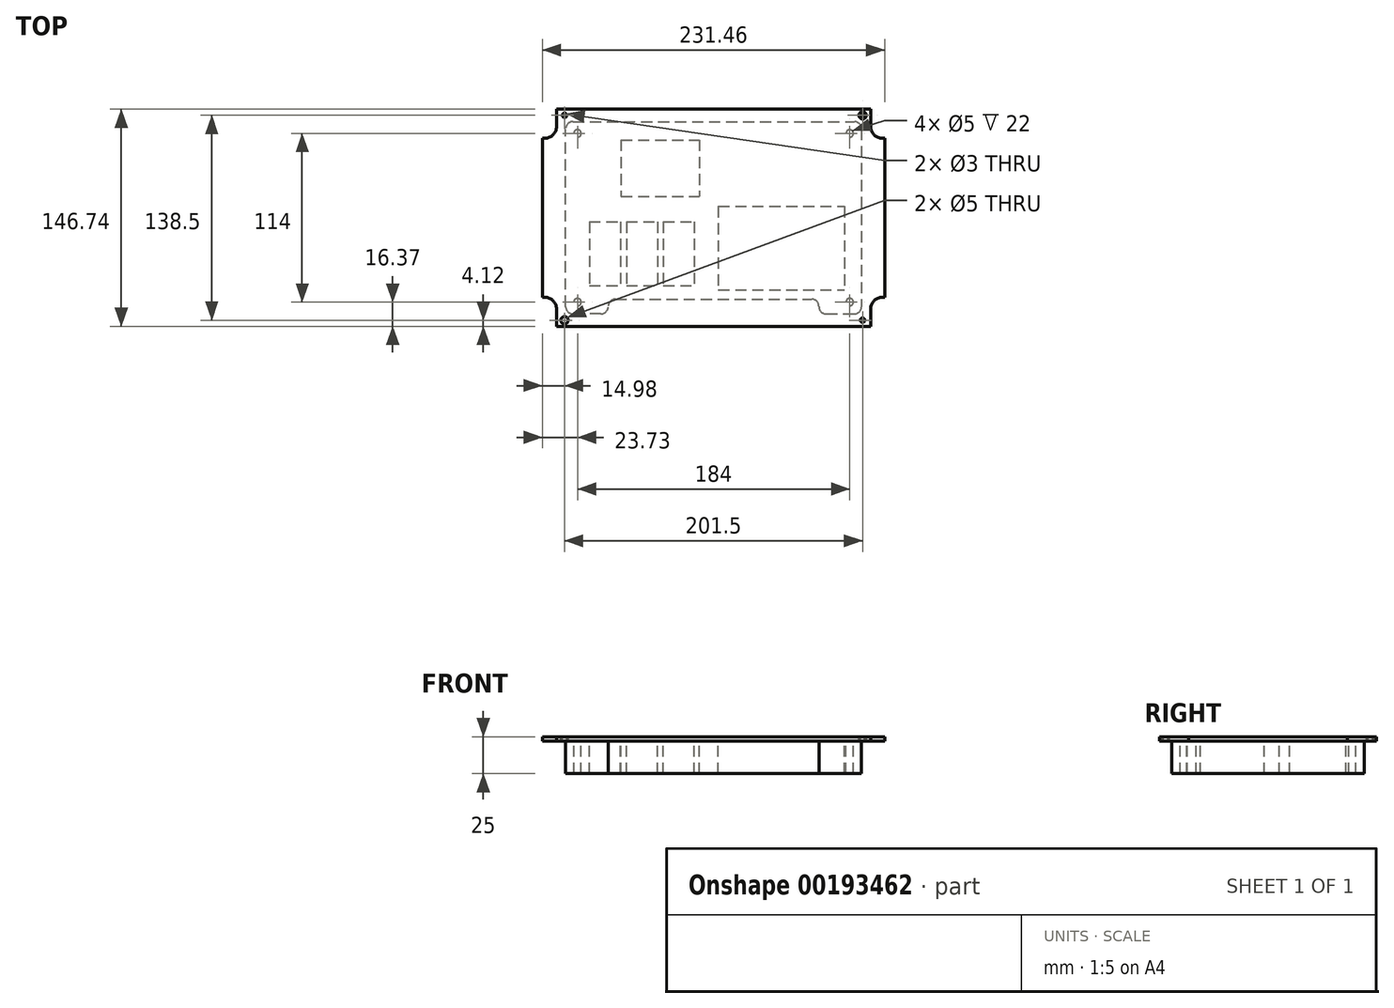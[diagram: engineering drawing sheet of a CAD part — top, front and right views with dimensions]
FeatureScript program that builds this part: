
annotation { "Feature Type Name" : "Feature", "Feature Type Description" : "" }
export const myFeature = defineFeature(function(context is Context, id is Id, definition is map)
    precondition{}
    {
        {
            var Q0;
            Q0=qCreatedBy(makeId("Top.planeOp"),FACE);
            var sketch = newSketch(context, id + "F0", { "sketchPlane" : qUnion([Q0])});
            skLineSegment(sketch, "E0.bottom", {"start": v(115.74, 73.37) * mm, "end": v(106.2, 73.37) * mm, "construction": true});
            skLineSegment(sketch, "E0.top", {"start": v(115.74, -73.37) * mm, "end": v(106.21, -73.37) * mm, "construction": true});
            skLineSegment(sketch, "E0.left", {"start": v(115.74, 73.37) * mm, "end": v(115.74, 53.68) * mm, "construction": true});
            skLineSegment(sketch, "E0.right", {"start": v(-115.74, 73.37) * mm, "end": v(-115.74, 53.68) * mm, "construction": true});
            skPoint(sketch, "E0.middle", {"position": v(0, 0) * mm});
            skLineSegment(sketch, "E1", {"start": v(-106.2, 73.37) * mm, "end": v(-106.2, 61.7) * mm});
            skLineSegment(sketch, "E2", {"start": v(-114.23, 53.68) * mm, "end": v(-115.74, 53.68) * mm});
            skLineSegment(sketch, "E3", {"start": v(0, 117.06) * mm, "end": v(0, -113.19) * mm, "construction": true});
            skPoint(sketch, "E3.startSnap0", {"position": v(0, 73.37) * mm});
            skPoint(sketch, "E4.visualSharp", {"position": v(-106.2, 53.68) * mm});
            skArc(sketch, "E4.filletArc", {"start": v(-114.23, 53.68) * mm, "mid": v(-108.56, 56.03) * mm, "end": v(-106.2, 61.7) * mm});
            skCircle(sketch, "E5", {"center": v(-100.75, 69.25) * mm, "radius": 1.5 * mm});
            skCircle(sketch, "E6.0", {"center": v(-100.75, 69.25) * mm, "radius": 2.5 * mm});
            skLineSegment(sketch, "E7", {"start": v(-150.85, 0) * mm, "end": v(151.7, 0) * mm, "construction": true});
            skLineSegment(sketch, "E8.MirrorCS", {"start": v(-114.23, -53.68) * mm, "end": v(-115.74, -53.68) * mm});
            skArc(sketch, "E9.MirrorCS", {"start": v(-114.24, -53.68) * mm, "mid": v(-108.56, -56.03) * mm, "end": v(-106.21, -61.7) * mm});
            skLineSegment(sketch, "E10.MirrorCS", {"start": v(-106.21, -73.37) * mm, "end": v(-106.21, -61.7) * mm});
            skCircle(sketch, "E11.MirrorC", {"center": v(-100.75, -69.25) * mm, "radius": 2.5 * mm});
            skCircle(sketch, "E12.MirrorC", {"center": v(-100.75, -69.25) * mm, "radius": 1.5 * mm});
            skLineSegment(sketch, "E13", {"start": v(-106.2, 73.37) * mm, "end": v(-115.74, 73.37) * mm, "construction": true});
            skLineSegment(sketch, "E14", {"start": v(-115.74, 53.68) * mm, "end": v(-115.74, -53.68) * mm});
            skLineSegment(sketch, "E15", {"start": v(-115.74, -53.68) * mm, "end": v(-115.74, -73.37) * mm, "construction": true});
            skLineSegment(sketch, "E16", {"start": v(-106.21, -73.37) * mm, "end": v(-115.74, -73.37) * mm, "construction": true});
            skCircle(sketch, "E17.MirrorC", {"center": v(100.75, 69.25) * mm, "radius": 1.5 * mm});
            skCircle(sketch, "E18.MirrorC", {"center": v(100.75, 69.25) * mm, "radius": 2.5 * mm});
            skLineSegment(sketch, "E19.MirrorCS", {"start": v(106.2, 73.37) * mm, "end": v(106.2, 61.7) * mm});
            skArc(sketch, "E20.MirrorCS", {"start": v(114.23, 53.68) * mm, "mid": v(108.56, 56.03) * mm, "end": v(106.2, 61.7) * mm});
            skLineSegment(sketch, "E21.MirrorCS", {"start": v(114.23, 53.68) * mm, "end": v(115.74, 53.68) * mm});
            skCircle(sketch, "E22.MirrorC", {"center": v(100.75, -69.25) * mm, "radius": 2.5 * mm});
            skLineSegment(sketch, "E23.MirrorCS", {"start": v(106.21, -73.37) * mm, "end": v(106.21, -61.7) * mm});
            skArc(sketch, "E24.MirrorCS", {"start": v(114.24, -53.68) * mm, "mid": v(108.56, -56.03) * mm, "end": v(106.21, -61.7) * mm});
            skLineSegment(sketch, "E25.MirrorCS", {"start": v(114.23, -53.68) * mm, "end": v(115.74, -53.68) * mm});
            skLineSegment(sketch, "E26", {"start": v(106.2, 73.37) * mm, "end": v(-106.2, 73.37) * mm});
            skLineSegment(sketch, "E27", {"start": v(115.74, 53.68) * mm, "end": v(115.74, -53.68) * mm});
            skLineSegment(sketch, "E28", {"start": v(115.74, -53.68) * mm, "end": v(115.74, -73.37) * mm, "construction": true});
            skLineSegment(sketch, "E29", {"start": v(106.21, -73.37) * mm, "end": v(-106.21, -73.37) * mm});
            skCircle(sketch, "E30.MirrorC", {"center": v(100.75, -69.25) * mm, "radius": 1.5 * mm});
            skLineSegment(sketch, "E31.bottom", {"start": v(80.54, -25.3) * mm, "end": v(80.54, 24.7) * mm});
            skLineSegment(sketch, "E31.top", {"start": v(107.54, -25.3) * mm, "end": v(107.54, 24.7) * mm});
            skLineSegment(sketch, "E31.left", {"start": v(80.54, -25.3) * mm, "end": v(107.54, -25.3) * mm});
            skLineSegment(sketch, "E31.right", {"start": v(80.54, 24.7) * mm, "end": v(107.54, 24.7) * mm});
            skPoint(sketch, "E32.orphan", {"position": v(89.06, 28.52) * mm});
            skLineSegment(sketch, "E33.bottom", {"start": v(-107.02, -25.24) * mm, "end": v(-107.02, 24.76) * mm});
            skLineSegment(sketch, "E33.top", {"start": v(-80.02, -25.24) * mm, "end": v(-80.02, 24.76) * mm});
            skLineSegment(sketch, "E33.left", {"start": v(-107.02, -25.24) * mm, "end": v(-80.02, -25.24) * mm});
            skLineSegment(sketch, "E33.right", {"start": v(-107.02, 24.76) * mm, "end": v(-80.02, 24.76) * mm});
            skSolve(sketch);
        }
        {
            var Q0;
            Q0=makeQuery(id+"F0.imprint","IMPRINT",FACE,{"disambiguationData":[TD([[makeQuery(id+"F0.imprint","IMPRINT",EDGE,{"derivedFrom":sQuery(id+"F0.wireOp",EDGE,"E1")}),1.0]])]});
            var Q1;
            Q1=makeQuery(id+"F0.imprint","IMPRINT",FACE,{"disambiguationData":[TD([[makeQuery(id+"F0.imprint","IMPRINT",EDGE,{"derivedFrom":sQuery(id+"F0.wireOp",EDGE,"E5")}),-1.0]])]});
            var Q2;
            Q2=makeQuery(id+"F0.imprint","IMPRINT",FACE,{"disambiguationData":[TD([[makeQuery(id+"F0.imprint","IMPRINT",EDGE,{"derivedFrom":sQuery(id+"F0.wireOp",EDGE,"E17.MirrorC")}),1.0]])]});
            var Q3;
            Q3=makeQuery(id+"F0.imprint","IMPRINT",FACE,{"disambiguationData":[TD([[makeQuery(id+"F0.imprint","IMPRINT",EDGE,{"derivedFrom":sQuery(id+"F0.wireOp",EDGE,"E11.MirrorC")}),-1.0]])]});
            var Q4;
            Q4=makeQuery(id+"F0.imprint","IMPRINT",FACE,{"disambiguationData":[TD([[makeQuery(id+"F0.imprint","IMPRINT",EDGE,{"derivedFrom":sQuery(id+"F0.wireOp",EDGE,"E22.MirrorC")}),1.0]])]});
            var Q5;
            Q5=makeQuery(id+"F0.imprint","IMPRINT",FACE,{"disambiguationData":[TD([[makeQuery(id+"F0.imprint","IMPRINT",EDGE,{"derivedFrom":sQuery(id+"F0.wireOp",EDGE,"E31.bottom")}),-1.0]])]});
            var Q6;
            Q6=makeQuery(id+"F0.imprint","IMPRINT",FACE,{"disambiguationData":[TD([[makeQuery(id+"F0.imprint","IMPRINT",EDGE,{"derivedFrom":sQuery(id+"F0.wireOp",EDGE,"E33.bottom")}),-1.0]])]});
            extrude(context, id + "F1", {"entities" : qUnion([Q0, Q1, Q2, Q3, Q4, Q5, Q6]), "oppositeDirection" : true, "depth" : 3 * mm});
        }
        {
            var Q0;
            Q0=makeQuery(id+"F1.opExtrude","CAP_FACE",FACE,{"disambiguationData":[OSD([sQuery(id+"F0.wireOp",EDGE,"E1"),sQuery(id+"F0.wireOp",EDGE,"E2"),sQuery(id+"F0.wireOp",EDGE,"E4.filletArc"),sQuery(id+"F0.wireOp",EDGE,"E5"),sQuery(id+"F0.wireOp",EDGE,"E8.MirrorCS"),sQuery(id+"F0.wireOp",EDGE,"E9.MirrorCS"),sQuery(id+"F0.wireOp",EDGE,"E10.MirrorCS"),sQuery(id+"F0.wireOp",EDGE,"E12.MirrorC"),sQuery(id+"F0.wireOp",EDGE,"E14"),sQuery(id+"F0.wireOp",EDGE,"E17.MirrorC"),sQuery(id+"F0.wireOp",EDGE,"E19.MirrorCS"),sQuery(id+"F0.wireOp",EDGE,"E20.MirrorCS"),sQuery(id+"F0.wireOp",EDGE,"E21.MirrorCS"),sQuery(id+"F0.wireOp",EDGE,"E23.MirrorCS"),sQuery(id+"F0.wireOp",EDGE,"E24.MirrorCS"),sQuery(id+"F0.wireOp",EDGE,"E25.MirrorCS"),sQuery(id+"F0.wireOp",EDGE,"E26"),sQuery(id+"F0.wireOp",EDGE,"E27"),sQuery(id+"F0.wireOp",EDGE,"E29"),sQuery(id+"F0.wireOp",EDGE,"E30.MirrorC")])],"isStart":true});
            var sketch = newSketch(context, id + "F2", { "sketchPlane" : qUnion([Q0])});
            skLineSegment(sketch, "E34.bottom", {"start": v(71.2, -61.7) * mm, "end": v(-71.2, -61.7) * mm});
            skLineSegment(sketch, "E34.top", {"start": v(71.2, 39.4) * mm, "end": v(-71.2, 39.4) * mm});
            skLineSegment(sketch, "E34.left", {"start": v(71.2, -61.7) * mm, "end": v(71.2, 39.4) * mm});
            skLineSegment(sketch, "E34.right", {"start": v(-71.2, -61.7) * mm, "end": v(-71.2, 39.4) * mm});
            skCircle(sketch, "E35", {"center": v(61.2, 35.4) * mm, "radius": 2.5 * mm});
            skCircle(sketch, "E36", {"center": v(-51.4, -51.7) * mm, "radius": 2.5 * mm});
            skLineSegment(sketch, "E37", {"start": v(-106.21, -61.7) * mm, "end": v(106.21, -61.7) * mm, "construction": true});
            skPoint(sketch, "E38", {"position": v(0, -61.7) * mm});
            skSolve(sketch);
        }
        {
            var Q0;
            Q0=makeQuery(id+"F2.imprint","IMPRINT",FACE,{"disambiguationData":[TD([[makeQuery(id+"F2.imprint","IMPRINT",EDGE,{"derivedFrom":sQuery(id+"F2.wireOp",EDGE,"E34.bottom")}),1.0]])]});
            var sketch = newSketch(context, id + "F3", { "sketchPlane" : qUnion([Q0])});
            skLineSegment(sketch, "E39.top", {"start": v(76.2, -65) * mm, "end": v(95, -65) * mm});
            skLineSegment(sketch, "E39.right", {"start": v(100, 0) * mm, "end": v(100, -60) * mm});
            skLineSegment(sketch, "E40.MirrorCS", {"start": v(0, 65) * mm, "end": v(95, 65) * mm});
            skLineSegment(sketch, "E41.MirrorCS", {"start": v(100, 0) * mm, "end": v(100, 60) * mm});
            skLineSegment(sketch, "E42.MirrorCS", {"start": v(0, 65) * mm, "end": v(-95, 65) * mm});
            skLineSegment(sketch, "E43.MirrorCS", {"start": v(-100, 0) * mm, "end": v(-100, 60) * mm});
            skLineSegment(sketch, "E44.MirrorCS", {"start": v(-100, 0) * mm, "end": v(-100, -60) * mm});
            skLineSegment(sketch, "E45.MirrorCS", {"start": v(-76.2, -65) * mm, "end": v(-95, -65) * mm});
            skCircle(sketch, "E46", {"center": v(-92, 57) * mm, "radius": 2.5 * mm});
            skCircle(sketch, "E47.MirrorC", {"center": v(92, 57) * mm, "radius": 2.5 * mm});
            skCircle(sketch, "E48.MirrorC", {"center": v(-92, -57) * mm, "radius": 2.5 * mm});
            skCircle(sketch, "E49.MirrorC", {"center": v(92, -57) * mm, "radius": 2.5 * mm});
            skCircle(sketch, "E50.0", {"center": v(-92, 57) * mm, "radius": 1.5 * mm});
            skCircle(sketch, "E51.MirrorC", {"center": v(92, 57) * mm, "radius": 1.5 * mm});
            skCircle(sketch, "E52.MirrorC", {"center": v(-92, -57) * mm, "radius": 1.5 * mm});
            skCircle(sketch, "E53.MirrorC", {"center": v(92, -57) * mm, "radius": 1.5 * mm});
            skPoint(sketch, "E54.visualSharp", {"position": v(100, 65) * mm});
            skArc(sketch, "E54.filletArc", {"start": v(100, 60) * mm, "mid": v(98.54, 63.54) * mm, "end": v(95, 65) * mm});
            skPoint(sketch, "E55.visualSharp", {"position": v(100, -65) * mm});
            skArc(sketch, "E55.filletArc", {"start": v(95, -65) * mm, "mid": v(98.54, -63.54) * mm, "end": v(100, -60) * mm});
            skPoint(sketch, "E56.visualSharp", {"position": v(-100, -65) * mm});
            skArc(sketch, "E56.filletArc", {"start": v(-100, -60) * mm, "mid": v(-98.54, -63.54) * mm, "end": v(-95, -65) * mm});
            skPoint(sketch, "E57.visualSharp", {"position": v(-100, 65) * mm});
            skArc(sketch, "E57.filletArc", {"start": v(-95, 65) * mm, "mid": v(-98.54, 63.54) * mm, "end": v(-100, 60) * mm});
            skLineSegment(sketch, "E58.0", {"start": v(-71.2, -61.7) * mm, "end": v(-71.2, -55) * mm, "construction": true});
            skLineSegment(sketch, "E59.0", {"start": v(71.2, -61.7) * mm, "end": v(71.2, -55) * mm, "construction": true});
            skLineSegment(sketch, "E60", {"start": v(-71.2, -60) * mm, "end": v(-71.2, -60) * mm});
            skLineSegment(sketch, "E61", {"start": v(-66.2, -55) * mm, "end": v(66.2, -55) * mm});
            skLineSegment(sketch, "E62", {"start": v(71.2, -60) * mm, "end": v(71.2, -60) * mm});
            skPoint(sketch, "E63.orphan", {"position": v(0, -65) * mm});
            skPoint(sketch, "E64.visualSharp", {"position": v(-71.2, -65) * mm});
            skArc(sketch, "E64.filletArc", {"start": v(-76.2, -65) * mm, "mid": v(-72.66, -63.54) * mm, "end": v(-71.2, -60) * mm});
            skPoint(sketch, "E65.visualSharp", {"position": v(-71.2, -55) * mm});
            skArc(sketch, "E65.filletArc", {"start": v(-66.2, -55) * mm, "mid": v(-69.74, -56.46) * mm, "end": v(-71.2, -60) * mm});
            skPoint(sketch, "E66.visualSharp", {"position": v(71.2, -55) * mm});
            skArc(sketch, "E66.filletArc", {"start": v(71.2, -60) * mm, "mid": v(69.74, -56.46) * mm, "end": v(66.2, -55) * mm});
            skPoint(sketch, "E67.visualSharp", {"position": v(71.2, -65) * mm});
            skArc(sketch, "E67.filletArc", {"start": v(71.2, -60) * mm, "mid": v(72.66, -63.54) * mm, "end": v(76.2, -65) * mm});
            skLineSegment(sketch, "E68.bottom", {"start": v(-83.98, -2.7) * mm, "end": v(-62.98, -2.7) * mm});
            skLineSegment(sketch, "E68.top", {"start": v(-83.98, -45.8) * mm, "end": v(-62.98, -45.8) * mm});
            skLineSegment(sketch, "E68.left", {"start": v(-83.98, -2.7) * mm, "end": v(-83.98, -45.8) * mm});
            skLineSegment(sketch, "E68.right", {"start": v(-62.98, -2.7) * mm, "end": v(-62.98, -45.8) * mm});
            skLineSegment(sketch, "E69.1.0.0", {"start": v(-58.98, -45.8) * mm, "end": v(-37.98, -45.8) * mm});
            skLineSegment(sketch, "E69.1.0.1", {"start": v(-58.98, -2.7) * mm, "end": v(-58.98, -45.8) * mm});
            skLineSegment(sketch, "E69.1.0.2", {"start": v(-58.98, -2.7) * mm, "end": v(-37.98, -2.7) * mm});
            skLineSegment(sketch, "E69.1.0.3", {"start": v(-37.98, -2.7) * mm, "end": v(-37.98, -45.8) * mm});
            skLineSegment(sketch, "E69.2.0.0", {"start": v(-33.98, -45.8) * mm, "end": v(-12.98, -45.8) * mm});
            skLineSegment(sketch, "E69.2.0.1", {"start": v(-33.98, -2.7) * mm, "end": v(-33.98, -45.8) * mm});
            skLineSegment(sketch, "E69.2.0.2", {"start": v(-33.98, -2.7) * mm, "end": v(-12.98, -2.7) * mm});
            skLineSegment(sketch, "E69.2.0.3", {"start": v(-12.98, -2.7) * mm, "end": v(-12.98, -45.8) * mm});
            skLineSegment(sketch, "E69.direction1", {"start": v(-83.98, -45.8) * mm, "end": v(-58.98, -45.8) * mm, "construction": true});
            skLineSegment(sketch, "E70.bottom", {"start": v(3.2, 7.7) * mm, "end": v(88.4, 7.7) * mm});
            skLineSegment(sketch, "E70.top", {"start": v(3.2, -48.7) * mm, "end": v(88.4, -48.7) * mm});
            skLineSegment(sketch, "E70.left", {"start": v(3.2, 7.7) * mm, "end": v(3.2, -48.7) * mm});
            skLineSegment(sketch, "E70.right", {"start": v(88.4, 7.7) * mm, "end": v(88.4, -48.7) * mm});
            skLineSegment(sketch, "E71.bottom", {"start": v(-62.5, 52.65) * mm, "end": v(-9.5, 52.65) * mm});
            skLineSegment(sketch, "E71.top", {"start": v(-62.5, 14.55) * mm, "end": v(-9.5, 14.55) * mm});
            skLineSegment(sketch, "E71.left", {"start": v(-62.5, 52.65) * mm, "end": v(-62.5, 14.55) * mm});
            skLineSegment(sketch, "E71.right", {"start": v(-9.5, 52.65) * mm, "end": v(-9.5, 14.55) * mm});
            skCircle(sketch, "E72", {"center": v(-59, 48.25) * mm, "radius": 1.5 * mm});
            skLineSegment(sketch, "E73", {"start": v(-62.5, 33.6) * mm, "end": v(-9.5, 33.6) * mm, "construction": true});
            skCircle(sketch, "E74.1.0.0", {"center": v(-13, 48.25) * mm, "radius": 1.5 * mm});
            skLineSegment(sketch, "E74.direction1", {"start": v(-59, 48.25) * mm, "end": v(-13, 48.25) * mm, "construction": true});
            skCircle(sketch, "E75.MirrorC", {"center": v(-59, 18.95) * mm, "radius": 1.5 * mm});
            skCircle(sketch, "E76.MirrorC", {"center": v(-13, 18.95) * mm, "radius": 1.5 * mm});
            skSolve(sketch);
        }
        {
            var Q0;
            Q0 = qSketchRegion(id + "F3", true);
            extrude(context, id + "F4", {"entities" : qUnion([Q0]), "operationType" : NewBodyOperationType.ADD, "oppositeDirection" : true, "depth" : 25 * mm});
        }
    });
